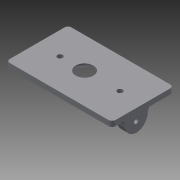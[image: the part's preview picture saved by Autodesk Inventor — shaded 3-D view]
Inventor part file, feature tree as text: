
AUTODESK INVENTOR PART (.ipt)
format: ipt  version: 2014 (Build 180170000, 170)  size: 161,280 bytes
history: native  units: mm
features: extrude x8, sketch x8, reference x3, fillet x2, chamfer x2
ambient origin geometry x8: Origin, YZ Plane, XZ Plane, XY Plane, X Axis, Y Axis, Z Axis, Center Point
bodies: Solid1 (feature_tree)
feature tree (23):
  extrude  "Extrusion1"  Depth=3.0mm
  extrude  "Extrusion2"  Depth=13.0mm TaperAngle=0.0deg
  extrude  "Extrusion3"  Depth=7.0mm TaperAngle=0.0deg
  fillet  "Fillet1"  Radius=7.0mm
  fillet  "Fillet2"  Radius=7.0mm
  extrude  "Extrusion4"  Depth=3.0mm
  chamfer  "Chamfer1"  Distance=10.0mm
  extrude  "Extrusion5"  Depth=10.0mm
  chamfer  "Chamfer2"  Distance=10.0mm
  sketch  "Sketch6"  dims[d16=1.0mm d17=2.0mm d18=45.0deg d19=10.0mm d20=10.0mm d21=0.0mm]
  extrude  "Extrusion6"  Depth=2.0mm
  extrude  "Extrusion7"  Depth=4.2mm
  extrude  "Extrusion8"  Depth=4.2mm TaperAngle=0.0deg
  sketch  "Sketch1"  dims[d0=3.0mm d1=0.0mm d2=0.8mm]
  reference  "Reference1"
  sketch  "Sketch2"  dims[d3=0.8mm d4=13.0mm d5=0.0mm]
  reference  "Reference2"
  sketch  "Sketch3"  dims[d6=2.2mm d7=15.0mm d8=0.0mm d9=7.0mm d10=7.0mm]
  reference  "Reference3"
  sketch  "Sketch4"  dims[d11=34.0mm d12=3.0mm]
  sketch  "Sketch5"  dims[d13=3.0mm d14=10.0mm d15=0.0mm]
  sketch  "Sketch7"  dims[d22=2.0mm d23=2.0mm d24=45.0deg d25=8.2mm]
  sketch  "Sketch8"  dims[d26=2.4mm d27=7.3mm d28=4.2mm d29=0.0mm d30=4.2mm d31=0.0mm d32=4.2mm d33=0.0mm]
